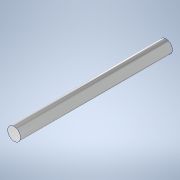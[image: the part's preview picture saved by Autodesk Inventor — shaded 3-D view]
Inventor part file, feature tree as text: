
AUTODESK INVENTOR PART (.ipt)
format: ipt  version: 2020.3 (Build 243373000, 373)  size: 92,672 bytes
history: native  units: mm
features: other x1, extrude x1, sketch x1
ambient origin geometry x8: Origin, YZ Plane, XZ Plane, XY Plane, X Axis, Y Axis, Z Axis, Center Point
bodies: Body1 (feature_tree)
feature tree (3):
  other  "ソリッド1"
  extrude  "押し出し1"  Depth=6.0mm
  sketch  "スケッチ1"
